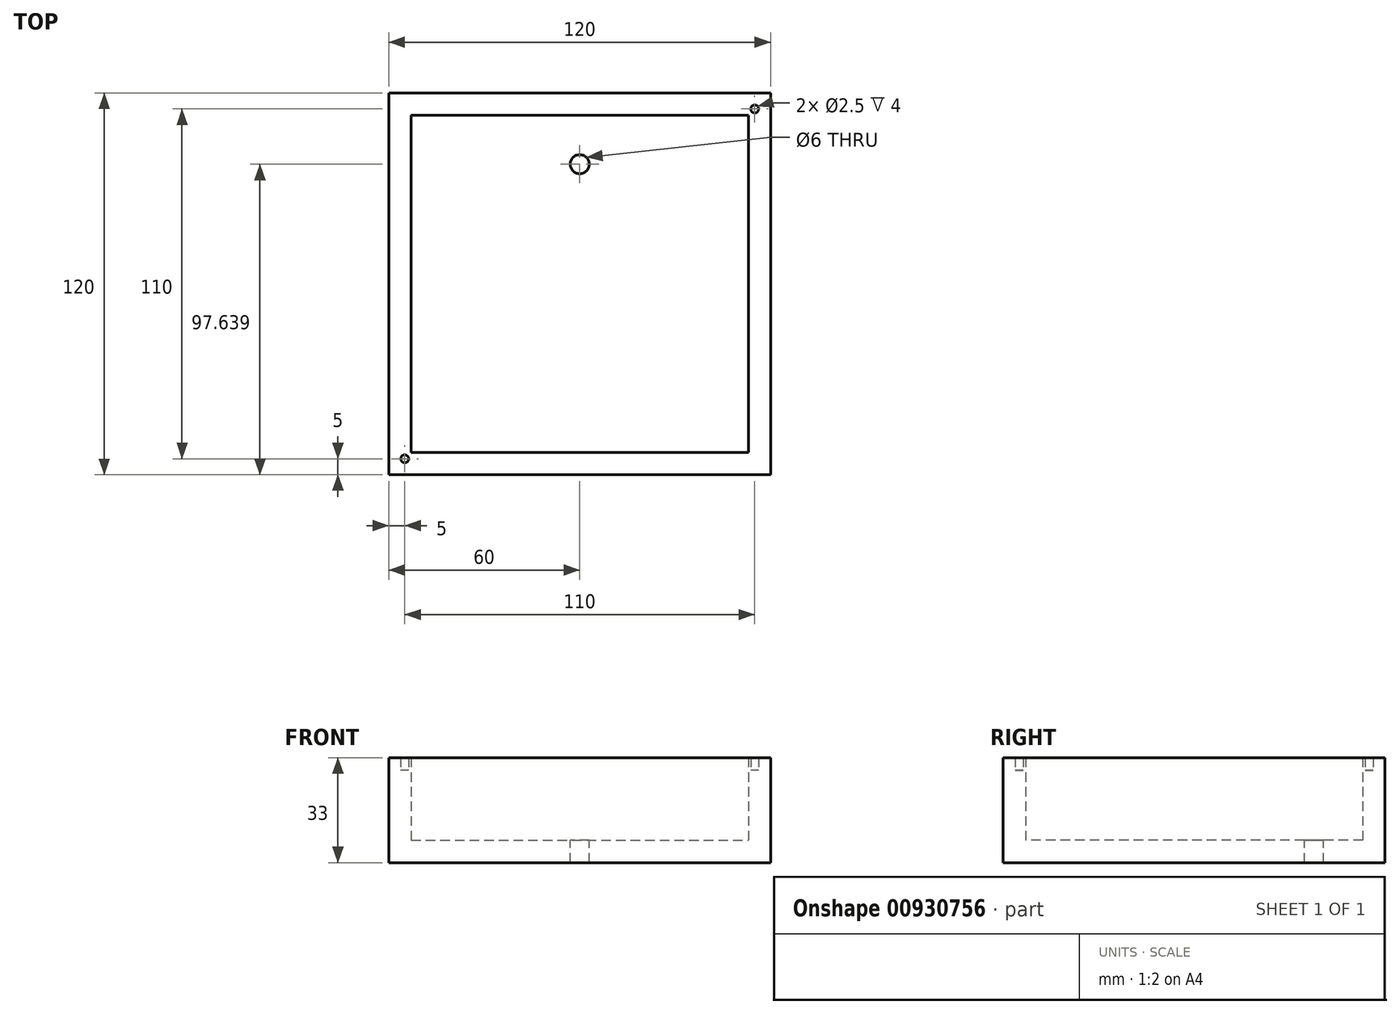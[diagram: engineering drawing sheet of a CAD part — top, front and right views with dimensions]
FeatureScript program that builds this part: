
annotation { "Feature Type Name" : "Feature", "Feature Type Description" : "" }
export const myFeature = defineFeature(function(context is Context, id is Id, definition is map)
    precondition{}
    {
        {
            var Q0;
            Q0=qCreatedBy(makeId("Top.planeOp"),FACE);
            var sketch = newSketch(context, id + "F0", { "sketchPlane" : qUnion([Q0])});
            skLineSegment(sketch, "E0.bottom", {"start": v(-60, 60) * mm, "end": v(60, 60) * mm});
            skLineSegment(sketch, "E0.top", {"start": v(-60, -60) * mm, "end": v(60, -60) * mm});
            skLineSegment(sketch, "E0.left", {"start": v(-60, 60) * mm, "end": v(-60, -60) * mm});
            skLineSegment(sketch, "E0.right", {"start": v(60, 60) * mm, "end": v(60, -60) * mm});
            skPoint(sketch, "E0.middle", {"position": v(0, 0) * mm});
            skSolve(sketch);
        }
        {
            var Q0;
            Q0=makeQuery(id+"F0.imprint","IMPRINT",FACE,{"disambiguationData":[TD([[makeQuery(id+"F0.imprint","IMPRINT",EDGE,{"derivedFrom":sQuery(id+"F0.wireOp",EDGE,"E0.bottom")}),-1.0]])]});
            extrude(context, id + "F1", {"entities" : qUnion([Q0]), "depth" : 29 * mm, "offsetDistance" : 25 * mm});
        }
        {
            var Q0;
            Q0=makeQuery(id+"F1.opExtrude","CAP_FACE",FACE,{"disambiguationData":[OSD([sQuery(id+"F0.wireOp",EDGE,"E0.bottom"),sQuery(id+"F0.wireOp",EDGE,"E0.top"),sQuery(id+"F0.wireOp",EDGE,"E0.left"),sQuery(id+"F0.wireOp",EDGE,"E0.right")])],"isStart":false});
            shell(context, id + "F2", {"entities" : qUnion([Q0]), "thickness" : 7 * mm});
        }
        {
            var Q0;
            Q0=makeQuery(id+"F1.opExtrude","CAP_FACE",FACE,{"disambiguationData":[OSD([sQuery(id+"F0.wireOp",EDGE,"E0.bottom"),sQuery(id+"F0.wireOp",EDGE,"E0.top"),sQuery(id+"F0.wireOp",EDGE,"E0.left"),sQuery(id+"F0.wireOp",EDGE,"E0.right")])],"isStart":false});
            var sketch = newSketch(context, id + "F3", { "sketchPlane" : qUnion([Q0])});
            skLineSegment(sketch, "E1", {"start": v(-60, 60) * mm, "end": v(-55, 60) * mm});
            skLineSegment(sketch, "E2", {"start": v(-55, 60) * mm, "end": v(-55, 55) * mm});
            skCircle(sketch, "E3", {"center": v(-55, 55) * mm, "radius": 1.25 * mm});
            skCircle(sketch, "E4.MirrorC", {"center": v(55, 55) * mm, "radius": 1.25 * mm});
            skCircle(sketch, "E5.MirrorC", {"center": v(-55, -55) * mm, "radius": 1.25 * mm});
            skCircle(sketch, "E6.MirrorC", {"center": v(55, -55) * mm, "radius": 1.25 * mm});
            skSolve(sketch);
        }
        {
            var Q0;
            Q0=makeQuery(id+"F3.imprint","IMPRINT",FACE,{"disambiguationData":[TD([[makeQuery(id+"F3.imprint","IMPRINT",EDGE,{"derivedFrom":sQuery(id+"F3.wireOp",EDGE,"E3")}),1.0]])]});
            var Q1;
            Q1=makeQuery(id+"F3.imprint","IMPRINT",FACE,{"disambiguationData":[TD([[makeQuery(id+"F3.imprint","IMPRINT",EDGE,{"derivedFrom":sQuery(id+"F3.wireOp",EDGE,"E4.MirrorC")}),-1.0]])]});
            var Q2;
            Q2=makeQuery(id+"F3.imprint","IMPRINT",FACE,{"disambiguationData":[TD([[makeQuery(id+"F3.imprint","IMPRINT",EDGE,{"derivedFrom":sQuery(id+"F3.wireOp",EDGE,"E6.MirrorC")}),1.0]])]});
            var Q3;
            Q3=makeQuery(id+"F3.imprint","IMPRINT",FACE,{"disambiguationData":[TD([[makeQuery(id+"F3.imprint","IMPRINT",EDGE,{"derivedFrom":sQuery(id+"F3.wireOp",EDGE,"E5.MirrorC")}),-1.0]])]});
            extrude(context, id + "F4", {"entities" : qUnion([Q0, Q1, Q2, Q3]), "operationType" : NewBodyOperationType.ADD, "depth" : 4 * mm, "offsetDistance" : 25 * mm});
        }
        {
            var Q0;
            Q0=makeQuery(id+"F2.opShell","OFFSET_FACE",FACE,{"disambiguationData":[OSD([sQuery(id+"F0.wireOp",EDGE,"E0.bottom"),sQuery(id+"F0.wireOp",EDGE,"E0.top"),sQuery(id+"F0.wireOp",EDGE,"E0.left"),sQuery(id+"F0.wireOp",EDGE,"E0.right")])]});
            var sketch = newSketch(context, id + "F5", { "sketchPlane" : qUnion([Q0])});
            skCircle(sketch, "E7", {"center": v(0, 37.64) * mm, "radius": 3 * mm});
            skSolve(sketch);
        }
        {
            var Q0;
            Q0 = qSketchRegion(id + "F5", true);
            extrude(context, id + "F6", {"entities" : qUnion([Q0]), "operationType" : NewBodyOperationType.REMOVE, "oppositeDirection" : true, "depth" : 7 * mm, "offsetDistance" : 25 * mm});
        }
    });
